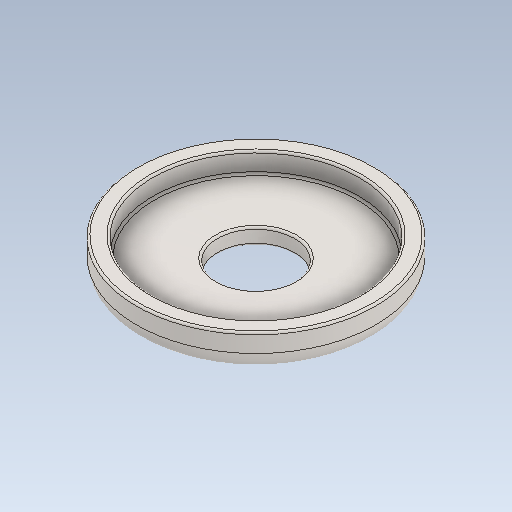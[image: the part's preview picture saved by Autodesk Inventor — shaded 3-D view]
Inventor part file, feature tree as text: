
AUTODESK INVENTOR PART (.ipt)
format: ipt  version: 2021 (Build 250183000, 183)  size: 173,056 bytes
history: mixed  units: in
note: dims shown in document units (in); Inventor stores cm internally (conversion verified against a paired STEP export)
features: revolve x1, imported_body x1
ambient origin geometry x8: Origin, YZ Plane, XZ Plane, XY Plane, X Axis, Y Axis, Z Axis, Center Point
bodies: Solid1 (imported_parasolid)
feature tree (2):
  revolve  "Revolve1"  [1 undecoded]
  imported_body  NMx_Import_Brep_tag  [imported B-rep: ~12 faces, bbox_mm=[0.0, 4.5, 10.0]]
note: 1 required parameter value undecoded (feature->parameter linkage not recoverable at this tier; creation-order binding heuristic only, values carry confidence <= 0.55)
